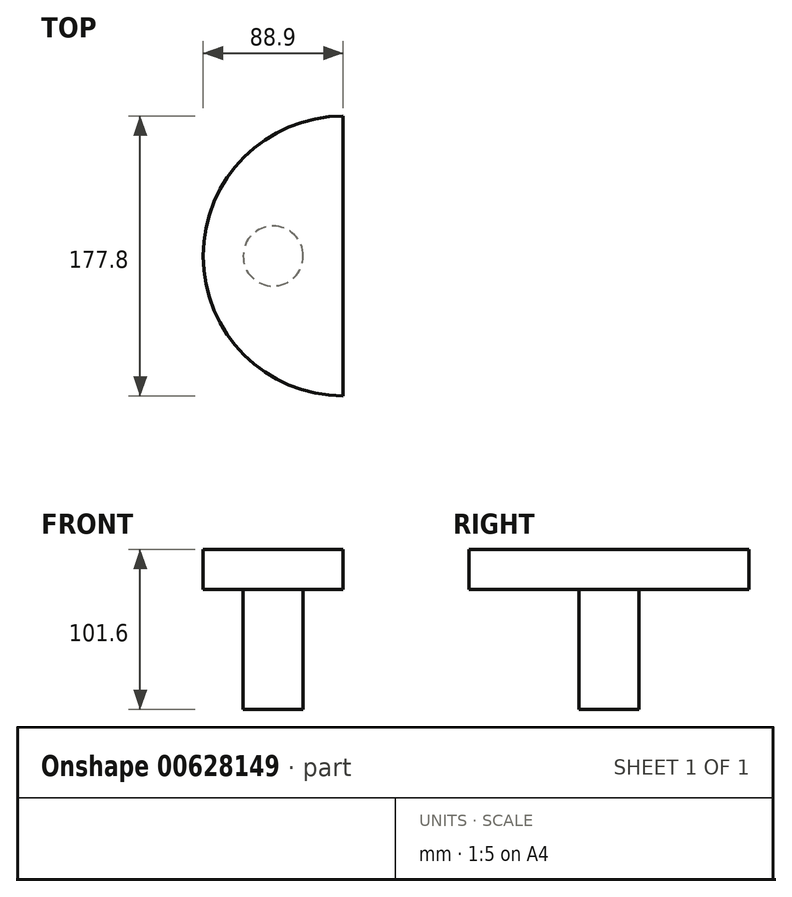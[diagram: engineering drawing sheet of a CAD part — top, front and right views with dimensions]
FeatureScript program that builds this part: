
annotation { "Feature Type Name" : "Feature", "Feature Type Description" : "" }
export const myFeature = defineFeature(function(context is Context, id is Id, definition is map)
    precondition{}
    {
        {
            var Q0;
            Q0=qCreatedBy(makeId("Top.planeOp"),FACE);
            var sketch = newSketch(context, id + "F0", { "sketchPlane" : qUnion([Q0])});
            skArc(sketch, "E0", {"start": v(0, 88.9) * mm, "mid": v(-88.9, 0) * mm, "end": v(0, -88.9) * mm});
            skLineSegment(sketch, "E1", {"start": v(0, 88.9) * mm, "end": v(0, -88.9) * mm});
            skSolve(sketch);
        }
        {
            var Q0;
            Q0=makeQuery(id+"F0.imprint","IMPRINT",FACE,{"disambiguationData":[TD([[makeQuery(id+"F0.imprint","IMPRINT",EDGE,{"derivedFrom":sQuery(id+"F0.wireOp",EDGE,"E0")}),1.0]])]});
            extrude(context, id + "F1", {"entities" : qUnion([Q0]), "depth" : 25.4 * mm, "offsetDistance" : 25.4 * mm});
        }
        {
            var Q0;
            Q0=makeQuery(id+"F1.opExtrude","CAP_FACE",FACE,{"disambiguationData":[OSD([sQuery(id+"F0.wireOp",EDGE,"E0"),sQuery(id+"F0.wireOp",EDGE,"E1")])],"isStart":true});
            var sketch = newSketch(context, id + "F2", { "sketchPlane" : qUnion([Q0])});
            skLineSegment(sketch, "E2", {"start": v(0, 0) * mm, "end": v(-88.9, 0) * mm});
            skCircle(sketch, "E3", {"center": v(-44.45, 0) * mm, "radius": 19.05 * mm});
            skSolve(sketch);
        }
        {
            var Q0;
            Q0 = qSketchRegion(id + "F2", true);
            extrude(context, id + "F3", {"entities" : qUnion([Q0]), "operationType" : NewBodyOperationType.ADD, "depth" : 76.2 * mm, "offsetDistance" : 25.4 * mm});
        }
    });
